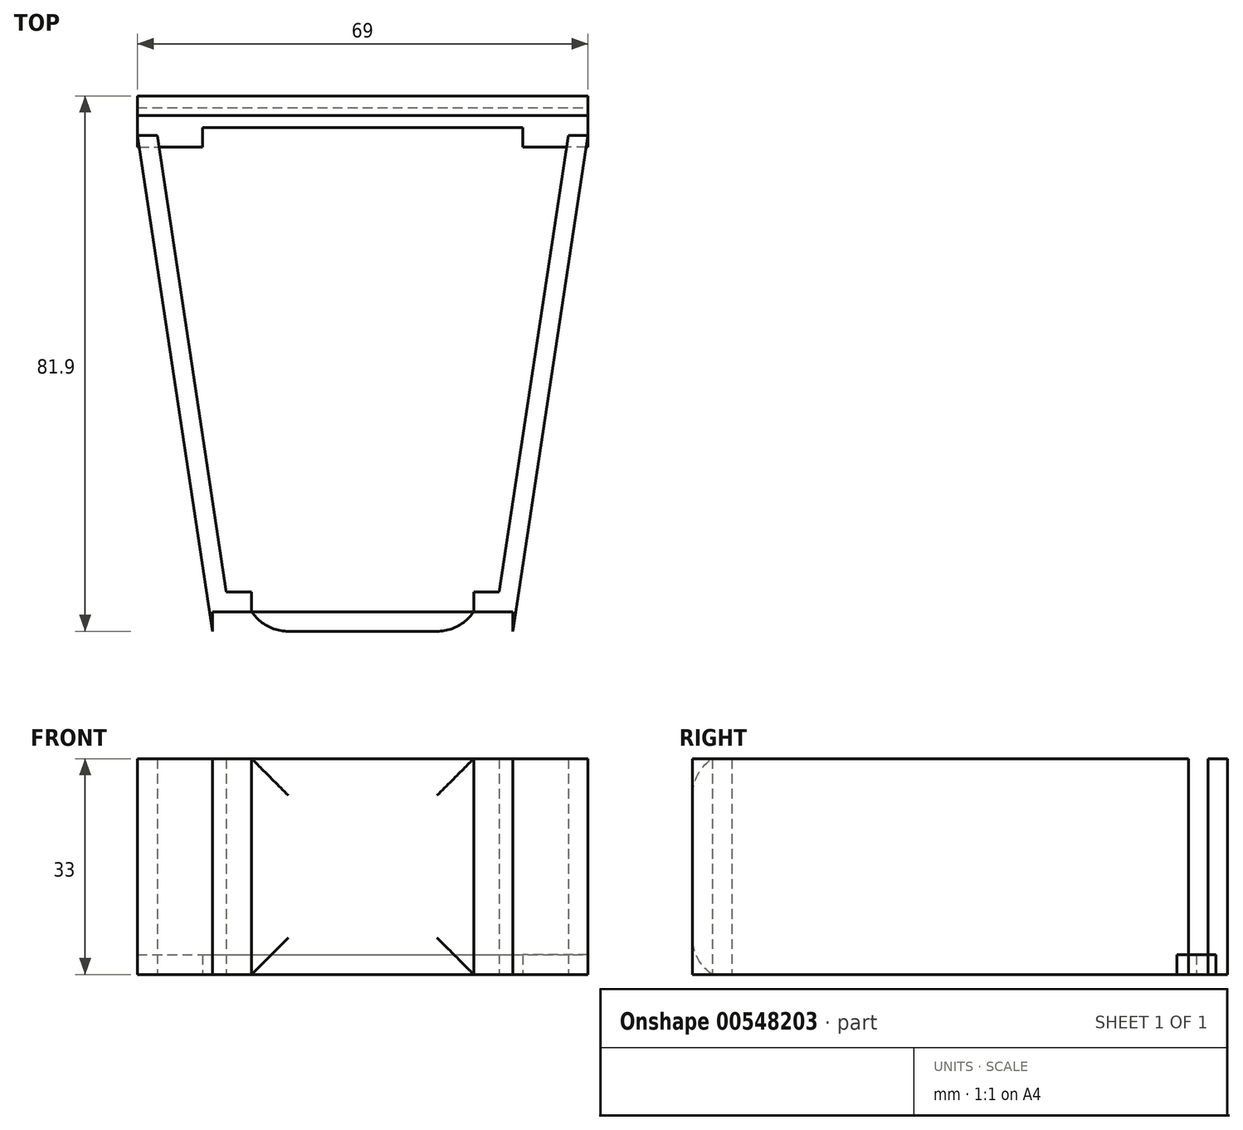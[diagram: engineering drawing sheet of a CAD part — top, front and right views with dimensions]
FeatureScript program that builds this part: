
annotation { "Feature Type Name" : "Feature", "Feature Type Description" : "" }
export const myFeature = defineFeature(function(context is Context, id is Id, definition is map)
    precondition{}
    {
        {
            var Q0;
            Q0=qCreatedBy(makeId("Top.planeOp"),FACE);
            var sketch = newSketch(context, id + "F0", { "sketchPlane" : qUnion([Q0])});
            skLineSegment(sketch, "E0.top", {"start": v(-34.5, 36.4) * mm, "end": v(34.5, 36.4) * mm});
            skPoint(sketch, "E0.middle", {"position": v(0, 0) * mm});
            skLineSegment(sketch, "E1.top", {"start": v(-34.5, 39.4) * mm, "end": v(34.5, 39.4) * mm});
            skLineSegment(sketch, "E1.left", {"start": v(-34.5, 36.4) * mm, "end": v(-34.5, 39.4) * mm});
            skLineSegment(sketch, "E1.right", {"start": v(34.5, 36.4) * mm, "end": v(34.5, 39.4) * mm});
            skLineSegment(sketch, "E2.bottom", {"start": v(-34.5, 36.4) * mm, "end": v(-24.5, 36.4) * mm});
            skLineSegment(sketch, "E2.top", {"start": v(-34.5, 33.4) * mm, "end": v(-24.5, 33.4) * mm});
            skLineSegment(sketch, "E2.left", {"start": v(-34.5, 36.4) * mm, "end": v(-34.5, 33.4) * mm});
            skLineSegment(sketch, "E2.right", {"start": v(-24.5, 36.4) * mm, "end": v(-24.5, 33.4) * mm});
            skLineSegment(sketch, "E3.bottom", {"start": v(34.5, 36.4) * mm, "end": v(24.5, 36.4) * mm});
            skLineSegment(sketch, "E3.top", {"start": v(34.5, 33.4) * mm, "end": v(24.5, 33.4) * mm});
            skLineSegment(sketch, "E3.left", {"start": v(34.5, 36.4) * mm, "end": v(34.5, 33.4) * mm});
            skLineSegment(sketch, "E3.right", {"start": v(24.5, 36.4) * mm, "end": v(24.5, 33.4) * mm});
            skLineSegment(sketch, "E4.bottom", {"start": v(-23, -42.5) * mm, "end": v(23, -42.5) * mm});
            skLineSegment(sketch, "E5", {"start": v(-34.5, 33.4) * mm, "end": v(-23, -42.5) * mm});
            skLineSegment(sketch, "E6", {"start": v(34.5, 33.4) * mm, "end": v(23, -42.5) * mm});
            skLineSegment(sketch, "E7.bottom", {"start": v(-23, -42.5) * mm, "end": v(-17, -42.5) * mm});
            skLineSegment(sketch, "E7.top", {"start": v(-23, -36.5) * mm, "end": v(-17, -36.5) * mm});
            skLineSegment(sketch, "E7.left", {"start": v(-23, -42.5) * mm, "end": v(-23, -36.5) * mm});
            skLineSegment(sketch, "E7.right", {"start": v(-17, -42.5) * mm, "end": v(-17, -36.5) * mm});
            skLineSegment(sketch, "E8.bottom", {"start": v(23, -42.5) * mm, "end": v(17, -42.5) * mm});
            skLineSegment(sketch, "E8.top", {"start": v(23, -36.5) * mm, "end": v(17, -36.5) * mm});
            skLineSegment(sketch, "E8.left", {"start": v(23, -42.5) * mm, "end": v(23, -36.5) * mm});
            skLineSegment(sketch, "E8.right", {"start": v(17, -42.5) * mm, "end": v(17, -36.5) * mm});
            skLineSegment(sketch, "E9.0", {"start": v(-31.53, 33.85) * mm, "end": v(-20.03, -42.05) * mm});
            skLineSegment(sketch, "E10.0", {"start": v(-23, -39.5) * mm, "end": v(23, -39.5) * mm});
            skLineSegment(sketch, "E11.0", {"start": v(31.53, 33.85) * mm, "end": v(20.03, -42.05) * mm});
            skSolve(sketch);
        }
        {
            var Q0;
            Q0=makeQuery(id+"F0.imprint","IMPRINT",FACE,{"disambiguationData":[TD([[makeQuery(id+"F0.imprint","IMPRINT",EDGE,{"derivedFrom":sQuery(id+"F0.wireOp",EDGE,"E0.top")}),1.0]])]});
            var Q1;
            Q1=makeQuery(id+"F0.imprint","IMPRINT",FACE,{"disambiguationData":[TD([[makeQuery(id+"F0.imprint","IMPRINT",EDGE,{"derivedFrom":sQuery(id+"F0.wireOp",EDGE,"E2.bottom")}),-1.0]])]});
            var Q2;
            Q2=makeQuery(id+"F0.imprint","IMPRINT",FACE,{"disambiguationData":[TD([[makeQuery(id+"F0.imprint","IMPRINT",EDGE,{"derivedFrom":sQuery(id+"F0.wireOp",EDGE,"E3.bottom")}),1.0]])]});
            var Q3;
            Q3=makeQuery(id+"F0.imprint","IMPRINT",FACE,{"disambiguationData":[TD([[makeQuery(id+"F0.imprint","IMPRINT",EDGE,{"derivedFrom":sQuery(id+"F0.wireOp",EDGE,"E7.bottom")}),1.0]])]});
            var Q4;
            {var subQ0=sQuery(id+"F0.wireOp",EDGE,"E7.right");var subQ1=sQuery(id+"F0.wireOp",EDGE,"E7.top");var subQ2=makeQuery(id+"F0.imprint","INTERSECT",VERTEX,{"derivedFrom":[subQ1,subQ0]});Q4=makeQuery(id+"F0.imprint","IMPRINT",FACE,{"disambiguationData":[TD([[makeQuery(id+"F0.imprint","IMPRINT",EDGE,{"disambiguationData":[TD([[subQ2,1.0]])],"derivedFrom":subQ1}),-1.0]])]});}
            var Q5;
            {var subQ0=sQuery(id+"F0.wireOp",EDGE,"E7.left");var subQ1=sQuery(id+"F0.wireOp",EDGE,"E7.top");var subQ2=makeQuery(id+"F0.imprint","INTERSECT",VERTEX,{"derivedFrom":[subQ1,subQ0]});Q5=makeQuery(id+"F0.imprint","IMPRINT",FACE,{"disambiguationData":[TD([[makeQuery(id+"F0.imprint","IMPRINT",EDGE,{"disambiguationData":[TD([[subQ2,-1.0]])],"derivedFrom":subQ1}),-1.0]])]});}
            var Q6;
            {var subQ0=sQuery(id+"F0.wireOp",EDGE,"E8.right");var subQ1=sQuery(id+"F0.wireOp",EDGE,"E8.top");var subQ2=makeQuery(id+"F0.imprint","INTERSECT",VERTEX,{"derivedFrom":[subQ1,subQ0]});Q6=makeQuery(id+"F0.imprint","IMPRINT",FACE,{"disambiguationData":[TD([[makeQuery(id+"F0.imprint","IMPRINT",EDGE,{"disambiguationData":[TD([[subQ2,1.0]])],"derivedFrom":subQ1}),1.0]])]});}
            var Q7;
            {var subQ5=sQuery(id+"F0.wireOp",EDGE,"E8.bottom");Q7=makeQuery(id+"F0.imprint","IMPRINT",FACE,{"disambiguationData":[TD([[makeQuery(id+"F0.imprint","IMPRINT",EDGE,{"derivedFrom":subQ5}),-1.0]])]});}
            var Q8;
            {var subQ0=sQuery(id+"F0.wireOp",EDGE,"E8.left");var subQ1=sQuery(id+"F0.wireOp",EDGE,"E8.top");var subQ2=makeQuery(id+"F0.imprint","INTERSECT",VERTEX,{"derivedFrom":[subQ1,subQ0]});Q8=makeQuery(id+"F0.imprint","IMPRINT",FACE,{"disambiguationData":[TD([[makeQuery(id+"F0.imprint","IMPRINT",EDGE,{"disambiguationData":[TD([[subQ2,-1.0]])],"derivedFrom":subQ1}),1.0]])]});}
            var Q9;
            {var subQ1=sQuery(id+"F0.wireOp",EDGE,"E6");Q9=makeQuery(id+"F0.imprint","IMPRINT",FACE,{"disambiguationData":[TD([[makeQuery(id+"F0.imprint","IMPRINT",EDGE,{"derivedFrom":subQ1}),-1.0]])]});}
            var Q10;
            {var subQ5=sQuery(id+"F0.wireOp",EDGE,"E5");Q10=makeQuery(id+"F0.imprint","IMPRINT",FACE,{"disambiguationData":[TD([[makeQuery(id+"F0.imprint","IMPRINT",EDGE,{"derivedFrom":subQ5}),1.0]])]});}
            var Q11;
            {var subQ0=sQuery(id+"F0.wireOp",EDGE,"E4.bottom");Q11=makeQuery(id+"F0.imprint","IMPRINT",FACE,{"disambiguationData":[TD([[makeQuery(id+"F0.imprint","IMPRINT",EDGE,{"derivedFrom":subQ0}),1.0]])]});}
            extrude(context, id + "F1", {"entities" : qUnion([Q0, Q1, Q2, Q3, Q4, Q5, Q6, Q7, Q8, Q9, Q10, Q11]), "depth" : 33 * mm, "offsetDistance" : 25 * mm});
        }
        {
            var Q0;
            Q0=qCreatedBy(makeId("Top.planeOp"),FACE);
            var sketch = newSketch(context, id + "F2", { "sketchPlane" : qUnion([Q0])});
            skLineSegment(sketch, "E12.top", {"start": v(-34.5, 34.61) * mm, "end": v(34.5, 34.61) * mm});
            skPoint(sketch, "E12.middle", {"position": v(0, -1.79) * mm});
            skLineSegment(sketch, "E13.top", {"start": v(-34.5, 37.61) * mm, "end": v(34.5, 37.61) * mm});
            skLineSegment(sketch, "E13.left", {"start": v(-34.5, 34.61) * mm, "end": v(-34.5, 37.61) * mm});
            skLineSegment(sketch, "E13.right", {"start": v(34.5, 34.61) * mm, "end": v(34.5, 37.61) * mm});
            skLineSegment(sketch, "E14.bottom", {"start": v(-34.5, 34.61) * mm, "end": v(-24.5, 34.61) * mm});
            skLineSegment(sketch, "E14.top", {"start": v(-34.5, 31.61) * mm, "end": v(-24.5, 31.61) * mm});
            skLineSegment(sketch, "E14.left", {"start": v(-34.5, 34.61) * mm, "end": v(-34.5, 31.61) * mm});
            skLineSegment(sketch, "E14.right", {"start": v(-24.5, 34.61) * mm, "end": v(-24.5, 31.61) * mm});
            skLineSegment(sketch, "E15.bottom", {"start": v(34.5, 34.61) * mm, "end": v(24.5, 34.61) * mm});
            skLineSegment(sketch, "E15.top", {"start": v(34.5, 31.61) * mm, "end": v(24.5, 31.61) * mm});
            skLineSegment(sketch, "E15.left", {"start": v(34.5, 34.61) * mm, "end": v(34.5, 31.61) * mm});
            skLineSegment(sketch, "E15.right", {"start": v(24.5, 34.61) * mm, "end": v(24.5, 31.61) * mm});
            skLineSegment(sketch, "E16.bottom", {"start": v(-23, -44.29) * mm, "end": v(23, -44.29) * mm});
            skLineSegment(sketch, "E17", {"start": v(-34.5, 31.61) * mm, "end": v(-23, -44.29) * mm});
            skLineSegment(sketch, "E18", {"start": v(34.5, 31.61) * mm, "end": v(23, -44.29) * mm});
            skLineSegment(sketch, "E19.bottom", {"start": v(-23, -44.29) * mm, "end": v(-17, -44.29) * mm});
            skLineSegment(sketch, "E19.top", {"start": v(-23, -38.29) * mm, "end": v(-17, -38.29) * mm});
            skLineSegment(sketch, "E19.left", {"start": v(-23, -44.29) * mm, "end": v(-23, -38.29) * mm});
            skLineSegment(sketch, "E19.right", {"start": v(-17, -44.29) * mm, "end": v(-17, -38.29) * mm});
            skLineSegment(sketch, "E20.bottom", {"start": v(23, -44.29) * mm, "end": v(17, -44.29) * mm});
            skLineSegment(sketch, "E20.top", {"start": v(23, -38.29) * mm, "end": v(17, -38.29) * mm});
            skLineSegment(sketch, "E20.left", {"start": v(23, -44.29) * mm, "end": v(23, -38.29) * mm});
            skLineSegment(sketch, "E20.right", {"start": v(17, -44.29) * mm, "end": v(17, -38.29) * mm});
            skLineSegment(sketch, "E21.0", {"start": v(-31.53, 32.06) * mm, "end": v(-20.03, -43.84) * mm});
            skLineSegment(sketch, "E22.0", {"start": v(-23, -41.29) * mm, "end": v(23, -41.29) * mm});
            skLineSegment(sketch, "E23.0", {"start": v(31.53, 32.06) * mm, "end": v(20.03, -43.84) * mm});
            skSolve(sketch);
        }
        {
            var Q0;
            Q0=makeQuery(id+"F2.imprint","IMPRINT",FACE,{"disambiguationData":[TD([[makeQuery(id+"F2.imprint","IMPRINT",EDGE,{"derivedFrom":sQuery(id+"F2.wireOp",EDGE,"E12.top")}),-1.0]])]});
            var Q1;
            Q1=makeQuery(id+"F2.imprint","IMPRINT",FACE,{"disambiguationData":[TD([[makeQuery(id+"F2.imprint","IMPRINT",EDGE,{"derivedFrom":sQuery(id+"F2.wireOp",EDGE,"E12.top")}),1.0]])]});
            var Q2;
            Q2=makeQuery(id+"F2.imprint","IMPRINT",FACE,{"disambiguationData":[TD([[makeQuery(id+"F2.imprint","IMPRINT",EDGE,{"derivedFrom":sQuery(id+"F2.wireOp",EDGE,"E15.bottom")}),1.0]])]});
            var Q3;
            Q3=makeQuery(id+"F2.imprint","IMPRINT",FACE,{"disambiguationData":[TD([[makeQuery(id+"F2.imprint","IMPRINT",EDGE,{"derivedFrom":sQuery(id+"F2.wireOp",EDGE,"E14.bottom")}),-1.0]])]});
            extrude(context, id + "F3", {"entities" : qUnion([Q0, Q1, Q2, Q3]), "depth" : 3 * mm, "offsetDistance" : 25 * mm});
        }
        {
            var Q0;
            Q0=makeQuery(id+"F1.opExtrude","SWEPT_FACE",FACE,{"disambiguationData":[OSD([sQuery(id+"F0.wireOp",EDGE,"E4.bottom"),sQuery(id+"F0.wireOp",EDGE,"E7.bottom"),sQuery(id+"F0.wireOp",EDGE,"E8.bottom")])]});
            var Q1;
            Q1=makeQuery(id+"F3.opExtrude","CAP_EDGE",EDGE,{"disambiguationData":[OSD([sQuery(id+"F2.wireOp",EDGE,"E22.0")])],"isStart":true});
            fillet(context, id + "F4", {"entities" : qUnion([Q0, Q1]), "radius" : 6.76 * mm, "tangentPropagation" : true, "allowEdgeOverflow" : false});
        }
    });
